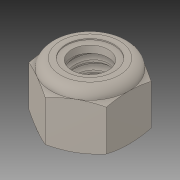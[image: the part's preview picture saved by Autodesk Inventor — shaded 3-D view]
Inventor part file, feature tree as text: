
AUTODESK INVENTOR PART (.ipt)
format: ipt  version: 2018 (Build 220112000, 112)  size: 273,920 bytes
history: native  units: in
note: dims shown in document units (in); Inventor stores cm internally (conversion verified against a paired STEP export)
features: other x1, revolve x1
ambient origin geometry x8: Origin, YZ Plane, XZ Plane, XY Plane, X Axis, Y Axis, Z Axis, Center Point
bodies: Solid1 (feature_tree), Solid2 (feature_tree)
feature tree (2):
  other  "Cut-Revolve4"
  revolve  "Revolve2"  [1 undecoded]
note: 1 required parameter value undecoded (feature->parameter linkage not recoverable at this tier; creation-order binding heuristic only, values carry confidence <= 0.55)
